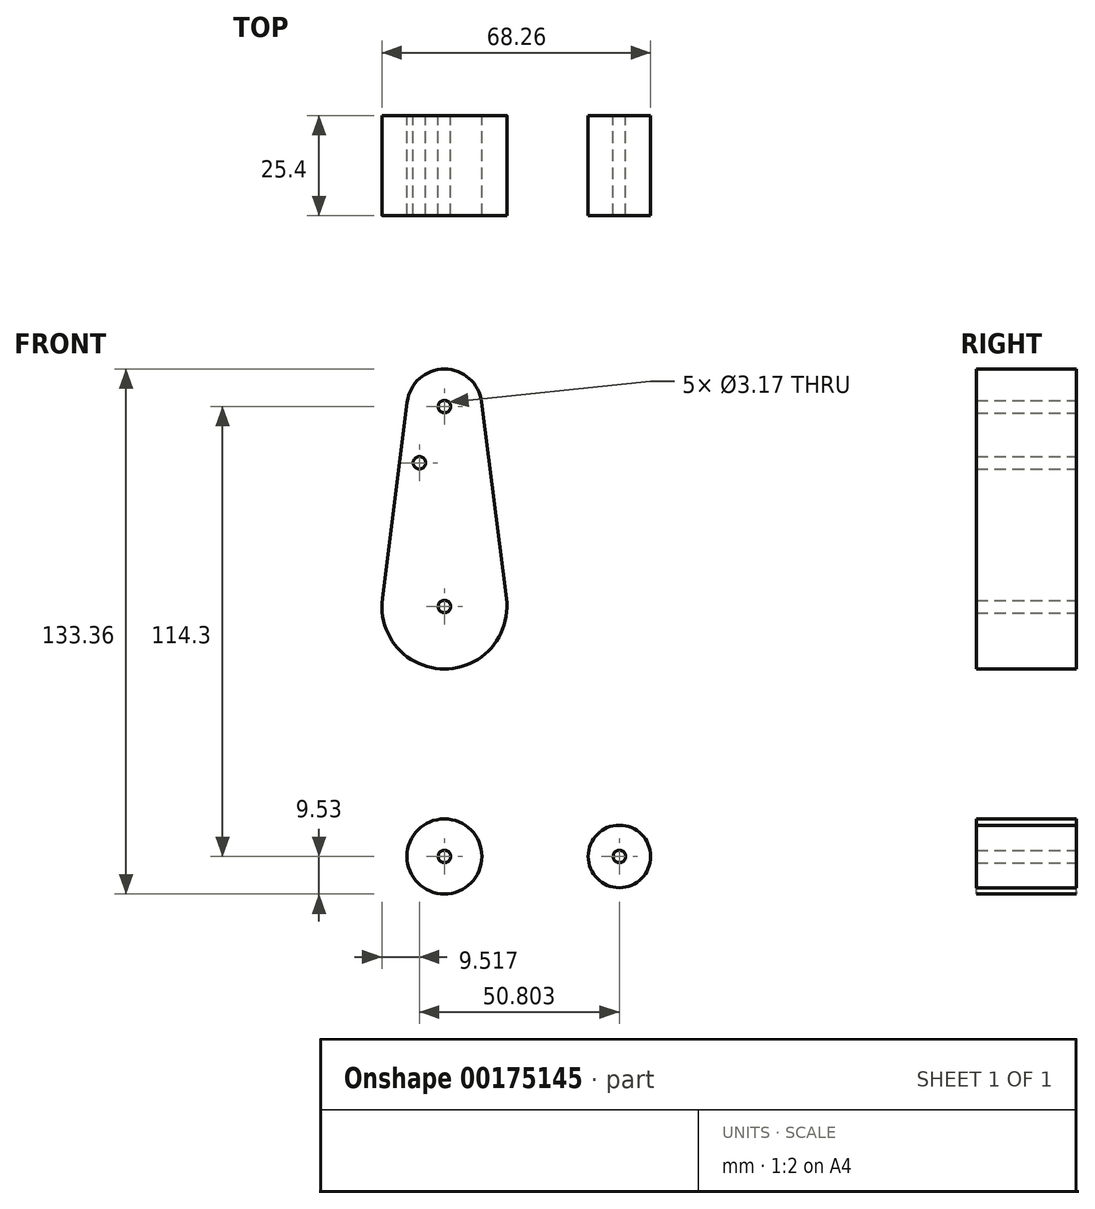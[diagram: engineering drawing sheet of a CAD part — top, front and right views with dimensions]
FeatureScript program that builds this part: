
annotation { "Feature Type Name" : "Feature", "Feature Type Description" : "" }
export const myFeature = defineFeature(function(context is Context, id is Id, definition is map)
    precondition{}
    {
        {
            var Q0;
            Q0=qCreatedBy(makeId("Front.planeOp"),FACE);
            var sketch = newSketch(context, id + "F0", { "sketchPlane" : qUnion([Q0])});
            skLineSegment(sketch, "E0", {"start": v(0, 0) * mm, "end": v(44.45, 0) * mm, "construction": true});
            skLineSegment(sketch, "E1", {"start": v(0, 0) * mm, "end": v(0, 63.5) * mm, "construction": true});
            skLineSegment(sketch, "E2", {"start": v(0, 63.5) * mm, "end": v(0, 114.3) * mm, "construction": true});
            skCircle(sketch, "E3", {"center": v(0, 114.3) * mm, "radius": 9.53 * mm});
            skCircle(sketch, "E4", {"center": v(0, 63.5) * mm, "radius": 15.88 * mm});
            skCircle(sketch, "E5", {"center": v(0, 0) * mm, "radius": 9.53 * mm});
            skCircle(sketch, "E6", {"center": v(44.45, 0) * mm, "radius": 7.94 * mm});
            skLineSegment(sketch, "E7", {"start": v(-9.45, 115.5) * mm, "end": v(-15.75, 65.48) * mm});
            skLineSegment(sketch, "E8", {"start": v(-15.8, 61.91) * mm, "end": v(-9.57, 0) * mm});
            skLineSegment(sketch, "E9", {"start": v(9.45, 115.5) * mm, "end": v(15.75, 65.48) * mm});
            skLineSegment(sketch, "E10", {"start": v(15.8, 61.9) * mm, "end": v(11.3, 17.6) * mm});
            skLineSegment(sketch, "E11", {"start": v(18.93, 8.85) * mm, "end": v(44.73, 7.93) * mm});
            skLineSegment(sketch, "E12", {"start": v(0, -9.53) * mm, "end": v(44.73, -7.93) * mm});
            skCircle(sketch, "E13", {"center": v(0, 114.3) * mm, "radius": 1.59 * mm});
            skCircle(sketch, "E14", {"center": v(-6.35, 100.03) * mm, "radius": 1.59 * mm});
            skCircle(sketch, "E15", {"center": v(0, 63.5) * mm, "radius": 1.59 * mm});
            skCircle(sketch, "E16", {"center": v(0, 0) * mm, "radius": 1.59 * mm});
            skCircle(sketch, "E17", {"center": v(44.45, 0) * mm, "radius": 1.59 * mm});
            skArc(sketch, "E18.filletArc", {"start": v(11.3, 17.6) * mm, "mid": v(13.22, 11.57) * mm, "end": v(18.93, 8.85) * mm});
            skSolve(sketch);
        }
        {
            var Q0;
            Q0 = qSketchRegion(id + "F0", true);
            extrude(context, id + "F1", {"entities" : qUnion([Q0]), "depth" : 25.4 * mm});
        }
    });
